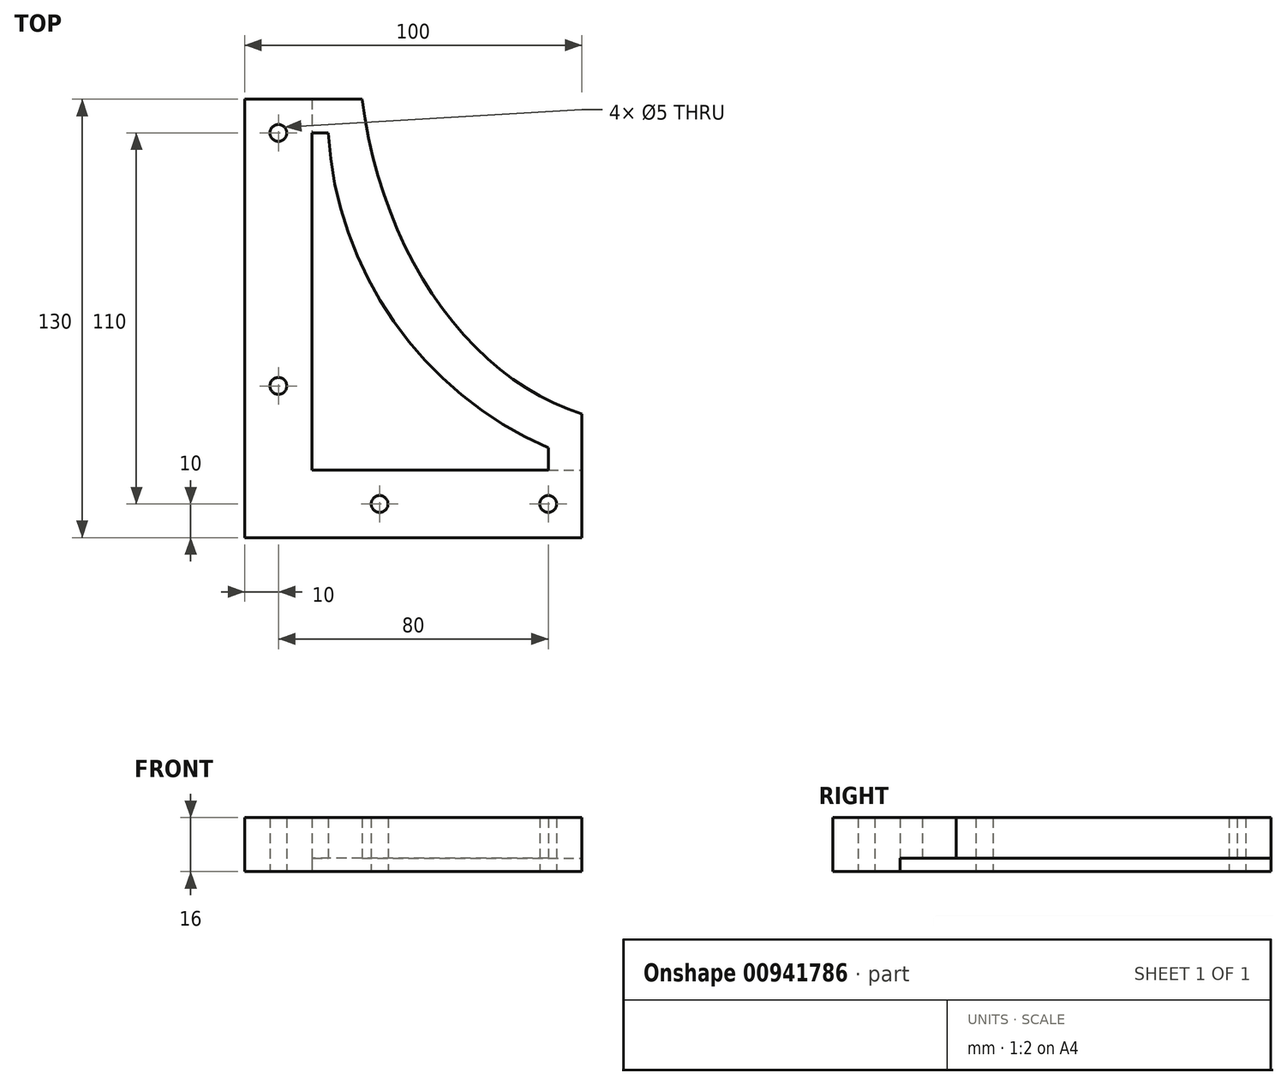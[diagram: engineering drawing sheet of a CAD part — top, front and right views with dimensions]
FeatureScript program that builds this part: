
annotation { "Feature Type Name" : "Feature", "Feature Type Description" : "" }
export const myFeature = defineFeature(function(context is Context, id is Id, definition is map)
    precondition{}
    {
        {
            var Q0;
            Q0=qCreatedBy(makeId("Top.planeOp"),FACE);
            var sketch = newSketch(context, id + "F0", { "sketchPlane" : qUnion([Q0])});
            skEllipticalArc(sketch, "E0", {});
            skLineSegment(sketch, "E1", {"start": v(-86.5, 0) * mm, "end": v(-86.5, -116.5) * mm});
            skPoint(sketch, "E1.endSnap0", {"position": v(0, -116.5) * mm});
            skLineSegment(sketch, "E2", {"start": v(-86.5, -116.5) * mm, "end": v(0, -116.5) * mm});
            skLineSegment(sketch, "E3", {"start": v(-86.5, 0) * mm, "end": v(-100, 0) * mm});
            skLineSegment(sketch, "E4", {"start": v(-100, 0) * mm, "end": v(-100, -130) * mm});
            skLineSegment(sketch, "E5", {"start": v(-100, -130) * mm, "end": v(0, -130) * mm});
            skLineSegment(sketch, "E6", {"start": v(0, -130) * mm, "end": v(0, -116.5) * mm});
            const initialGuessF0  = {"E0": [0, 0, 1, 0, 0.0865, 0.1165, 3.141592653589793, 4.71238898038469]};
            skSetInitialGuess(sketch, initialGuessF0);
            skSolve(sketch);
        }
        {
            var Q0;
            Q0=qSketchRegion(id+"F0",true);
            extrude(context, id + "F1", {"entities" : qUnion([Q0]), "depth" : 12 * mm, "offsetDistance" : 25 * mm});
        }
        {
            var Q0;
            Q0=makeQuery(id+"F1.opExtrude","SWEPT_FACE",FACE,{"disambiguationData":[OSD([sQuery(id+"F0.wireOp",EDGE,"E5")])]});
            var sketch = newSketch(context, id + "F2", { "sketchPlane" : qUnion([Q0])});
            skLineSegment(sketch, "E7.bottom", {"start": v(-100, 16) * mm, "end": v(0, 16) * mm});
            skLineSegment(sketch, "E7.top", {"start": v(-100, -4) * mm, "end": v(0, -4) * mm});
            skLineSegment(sketch, "E7.left", {"start": v(-100, 16) * mm, "end": v(-100, -4) * mm});
            skLineSegment(sketch, "E7.right", {"start": v(0, 16) * mm, "end": v(0, -4) * mm});
            skSolve(sketch);
        }
        {
            var Q0;
            Q0=qSketchRegion(id+"F2",true);
            extrude(context, id + "F3", {"entities" : qUnion([Q0]), "operationType" : NewBodyOperationType.ADD, "depth" : 5 * mm, "offsetDistance" : 25 * mm});
        }
        {
            var Q0;
            Q0=makeQuery(id+"F3.boolean.opBoolean","MERGE",FACE,{"derivedFrom":[makeQuery(id+"F1.opExtrude","SWEPT_FACE",FACE,{"disambiguationData":[OSD([sQuery(id+"F0.wireOp",EDGE,"E4")])]}),makeQuery(id+"F3.opExtrude","SWEPT_FACE",FACE,{"disambiguationData":[OSD([sQuery(id+"F2.wireOp",EDGE,"E7.left")])]})]});
            var sketch = newSketch(context, id + "F4", { "sketchPlane" : qUnion([Q0])});
            skLineSegment(sketch, "E8.bottom", {"start": v(135, 16) * mm, "end": v(0, 16) * mm});
            skLineSegment(sketch, "E8.top", {"start": v(135, -4) * mm, "end": v(0, -4) * mm});
            skLineSegment(sketch, "E8.left", {"start": v(135, 16) * mm, "end": v(135, -4) * mm});
            skLineSegment(sketch, "E8.right", {"start": v(0, 16) * mm, "end": v(0, -4) * mm});
            skSolve(sketch);
        }
        {
            var Q0;
            Q0=qSketchRegion(id+"F4",true);
            extrude(context, id + "F5", {"entities" : qUnion([Q0]), "operationType" : NewBodyOperationType.ADD, "depth" : 5 * mm, "offsetDistance" : 25 * mm});
        }
        {
            var Q0;
            Q0=makeQuery(id+"F5.boolean.opBoolean","MERGE",FACE,{"derivedFrom":[makeQuery(id+"F3.opExtrude","SWEPT_FACE",FACE,{"disambiguationData":[OSD([sQuery(id+"F2.wireOp",EDGE,"E7.bottom")])]}),makeQuery(id+"F5.opExtrude","SWEPT_FACE",FACE,{"disambiguationData":[OSD([sQuery(id+"F4.wireOp",EDGE,"E8.bottom")])]})]});
            var sketch = newSketch(context, id + "F6", { "sketchPlane" : qUnion([Q0])});
            skLineSegment(sketch, "E9", {"start": v(-105, 0) * mm, "end": v(-90, 0) * mm});
            skLineSegment(sketch, "E10", {"start": v(-90, 0) * mm, "end": v(-90, -120) * mm});
            skLineSegment(sketch, "E11", {"start": v(-90, -120) * mm, "end": v(0, -120) * mm});
            skLineSegment(sketch, "E12", {"start": v(0, -120) * mm, "end": v(0, -135) * mm});
            skLineSegment(sketch, "E13", {"start": v(0, -135) * mm, "end": v(-105, -135) * mm});
            skLineSegment(sketch, "E14", {"start": v(-105, -135) * mm, "end": v(-105, 0) * mm});
            skSolve(sketch);
        }
        {
            var Q0;
            Q0=makeQuery(id+"F5.boolean.opBoolean","MERGE",FACE,{"derivedFrom":[makeQuery(id+"F3.opExtrude","SWEPT_FACE",FACE,{"disambiguationData":[OSD([sQuery(id+"F2.wireOp",EDGE,"E7.top")])]}),makeQuery(id+"F5.opExtrude","SWEPT_FACE",FACE,{"disambiguationData":[OSD([sQuery(id+"F4.wireOp",EDGE,"E8.top")])]})]});
            var sketch = newSketch(context, id + "F7", { "sketchPlane" : qUnion([Q0])});
            skLineSegment(sketch, "E15", {"start": v(0, 150) * mm, "end": v(-120, 150) * mm});
            skLineSegment(sketch, "E16", {"start": v(-120, 150) * mm, "end": v(-120, 0) * mm});
            skLineSegment(sketch, "E17", {"start": v(-120, 0) * mm, "end": v(-105, 0) * mm});
            skLineSegment(sketch, "E18", {"start": v(-105, 0) * mm, "end": v(-105, 135) * mm});
            skLineSegment(sketch, "E19", {"start": v(-105, 135) * mm, "end": v(0, 135) * mm});
            skLineSegment(sketch, "E20", {"start": v(0, 135) * mm, "end": v(0, 150) * mm});
            skCircle(sketch, "E21", {"center": v(-110, 30) * mm, "radius": 2.5 * mm});
            skCircle(sketch, "E22", {"center": v(-110, 105) * mm, "radius": 2.5 * mm});
            skCircle(sketch, "E23", {"center": v(-80, 140) * mm, "radius": 2.5 * mm});
            skCircle(sketch, "E24", {"center": v(-30, 140) * mm, "radius": 2.5 * mm});
            skSolve(sketch);
        }
        {
            var Q0;
            Q0=qSketchRegion(id+"F7",true);
            extrude(context, id + "F8", {"entities" : qUnion([Q0]), "operationType" : NewBodyOperationType.ADD, "oppositeDirection" : true, "depth" : 25 * mm, "offsetDistance" : 25 * mm});
        }
        {
            var Q0;
            Q0=qSketchRegion(id+"F6",true);
            extrude(context, id + "F9", {"entities" : qUnion([Q0]), "operationType" : NewBodyOperationType.ADD, "depth" : 5 * mm, "offsetDistance" : 25 * mm});
        }
        {
            var Q0;
            Q0=qCreatedBy(makeId("Top.planeOp"),FACE);
            var sketch = newSketch(context, id + "F10", { "sketchPlane" : qUnion([Q0])});
            skLineSegment(sketch, "E25.bottom", {"start": v(0, 0) * mm, "end": v(-120, 0) * mm});
            skLineSegment(sketch, "E25.top", {"start": v(0, -20) * mm, "end": v(-120, -20) * mm});
            skLineSegment(sketch, "E25.left", {"start": v(0, 0) * mm, "end": v(0, -20) * mm});
            skLineSegment(sketch, "E25.right", {"start": v(-120, 0) * mm, "end": v(-120, -20) * mm});
            skLineSegment(sketch, "E26.bottom", {"start": v(0, 0) * mm, "end": v(-20, 0) * mm});
            skLineSegment(sketch, "E26.top", {"start": v(0, -150) * mm, "end": v(-20, -150) * mm});
            skLineSegment(sketch, "E26.left", {"start": v(0, 0) * mm, "end": v(0, -150) * mm});
            skLineSegment(sketch, "E26.right", {"start": v(-20, 0) * mm, "end": v(-20, -150) * mm});
            skSolve(sketch);
        }
        {
            var Q0;
            Q0=qSketchRegion(id+"F10",true);
            extrude(context, id + "F11", {"entities" : qUnion([Q0]), "operationType" : NewBodyOperationType.REMOVE, "endBound" : BoundingType.SYMMETRIC, "oppositeDirection" : true, "depth" : 50 * mm, "offsetDistance" : 25 * mm});
        }
        {
            var Q0;
            Q0=makeQuery(id+"F11.boolean.opBoolean","COPY",FACE,{"derivedFrom":makeQuery(id+"F11.opExtrude","SWEPT_FACE",FACE,{"disambiguationData":[OSD([sQuery(id+"F10.wireOp",EDGE,"E26.right")])]})});
            var sketch = newSketch(context, id + "F12", { "sketchPlane" : qUnion([Q0])});
            skLineSegment(sketch, "E27.bottom", {"start": v(-150, 21) * mm, "end": v(-20, 21) * mm});
            skLineSegment(sketch, "E27.top", {"start": v(-150, 12) * mm, "end": v(-20, 12) * mm});
            skLineSegment(sketch, "E27.left", {"start": v(-150, 21) * mm, "end": v(-150, 12) * mm});
            skLineSegment(sketch, "E27.right", {"start": v(-20, 21) * mm, "end": v(-20, 12) * mm});
            skSolve(sketch);
        }
        {
            var Q0;
            Q0=qSketchRegion(id+"F12",true);
            extrude(context, id + "F13", {"entities" : qUnion([Q0]), "operationType" : NewBodyOperationType.REMOVE, "endBound" : BoundingType.THROUGH_ALL, "oppositeDirection" : true, "depth" : 25 * mm, "offsetDistance" : 25 * mm});
        }
        {
            var Q0;
            Q0=makeQuery(id+"F1.opExtrude","CAP_FACE",FACE,{"disambiguationData":[OSD([sQuery(id+"F0.wireOp",EDGE,"E0"),sQuery(id+"F0.wireOp",EDGE,"E3"),sQuery(id+"F0.wireOp",EDGE,"E4"),sQuery(id+"F0.wireOp",EDGE,"E5"),sQuery(id+"F0.wireOp",EDGE,"E6")])],"isStart":true});
            var sketch = newSketch(context, id + "F14", { "sketchPlane" : qUnion([Q0])});
            skPoint(sketch, "E28.startSnap0", {"position": v(-20, 121.67) * mm});
            skLineSegment(sketch, "E29", {"start": v(-100, 130) * mm, "end": v(-100, 30) * mm});
            skLineSegment(sketch, "E30", {"start": v(-100, 30) * mm, "end": v(-95.22, 30) * mm});
            skLineSegment(sketch, "E31", {"start": v(-100, 130) * mm, "end": v(-30, 130) * mm});
            skLineSegment(sketch, "E32", {"start": v(-30, 130) * mm, "end": v(-30, 123.34) * mm});
            skArc(sketch, "E33", {"start": v(-30, 123.34) * mm, "mid": v(-75.82, 85.9) * mm, "end": v(-95.22, 30) * mm});
            skSolve(sketch);
        }
        {
            var Q0;
            Q0 = qSketchRegion(id + "F14", true);
            extrude(context, id + "F15", {"entities" : qUnion([Q0]), "operationType" : NewBodyOperationType.REMOVE, "endBound" : BoundingType.THROUGH_ALL, "oppositeDirection" : true, "depth" : 25 * mm, "offsetDistance" : 25 * mm});
        }
    });
